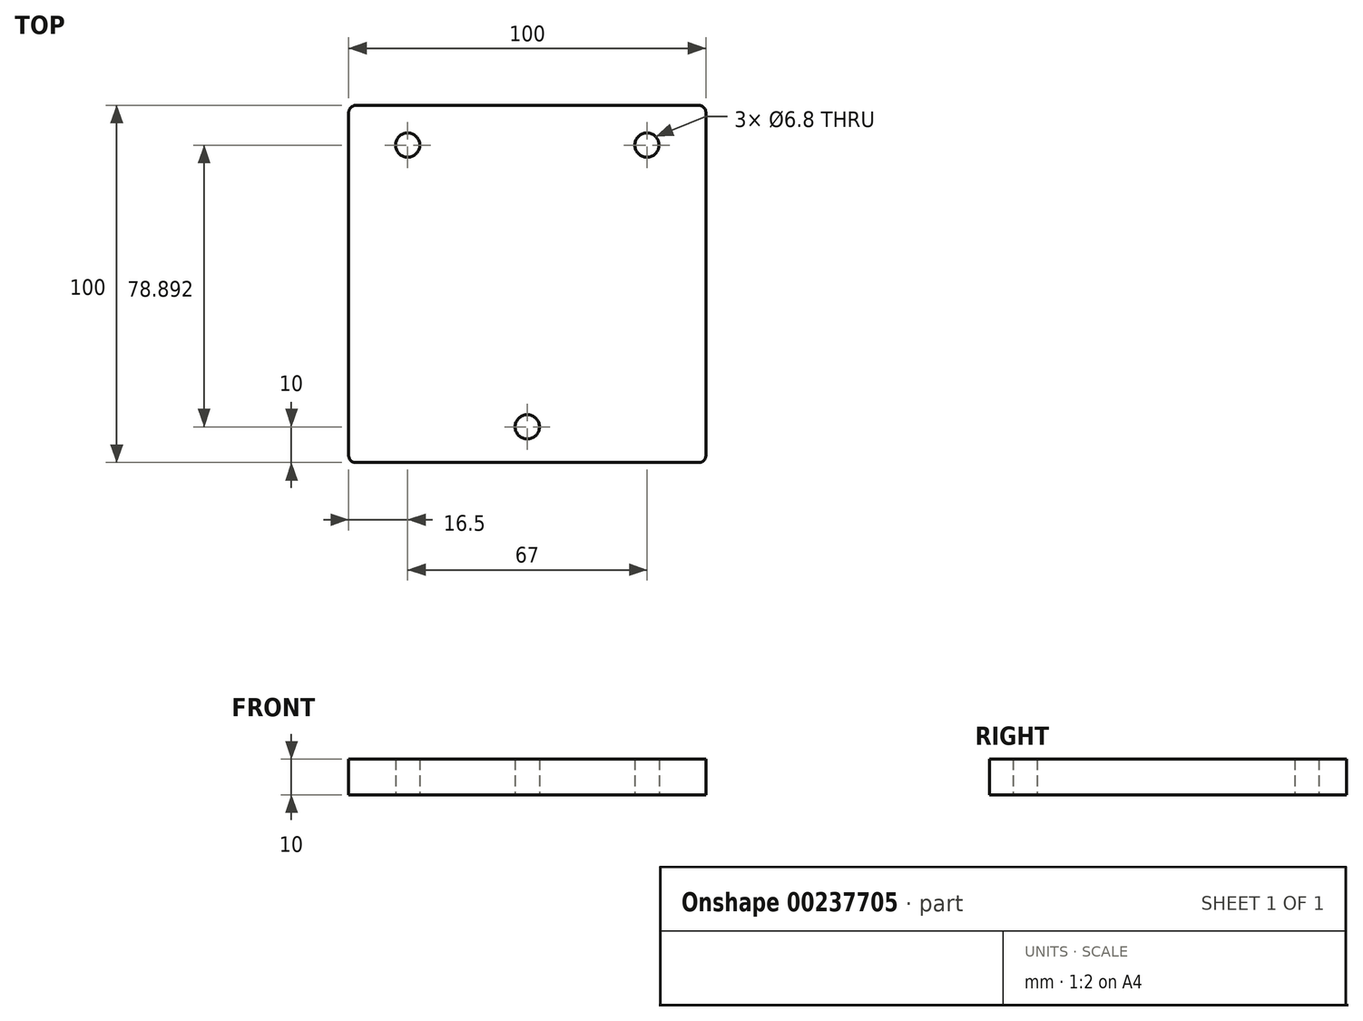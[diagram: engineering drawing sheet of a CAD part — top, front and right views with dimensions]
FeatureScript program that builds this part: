
annotation { "Feature Type Name" : "Feature", "Feature Type Description" : "" }
export const myFeature = defineFeature(function(context is Context, id is Id, definition is map)
    precondition{}
    {
        {
            var Q0;
            Q0=qCreatedBy(makeId("Top.planeOp"),FACE);
            var sketch = newSketch(context, id + "F0", { "sketchPlane" : qUnion([Q0])});
            skLineSegment(sketch, "E0.bottom", {"start": v(48, 50) * mm, "end": v(-48, 50) * mm});
            skLineSegment(sketch, "E0.top", {"start": v(48, -50) * mm, "end": v(-48, -50) * mm});
            skLineSegment(sketch, "E0.left", {"start": v(50, 48) * mm, "end": v(50, -48) * mm});
            skLineSegment(sketch, "E0.right", {"start": v(-50, 48) * mm, "end": v(-50, -48) * mm});
            skPoint(sketch, "E0.middle", {"position": v(0, 0) * mm});
            skPoint(sketch, "E1.visualSharp", {"position": v(-50, 50) * mm});
            skArc(sketch, "E1.filletArc", {"start": v(-48, 50) * mm, "mid": v(-49.41, 49.41) * mm, "end": v(-50, 48) * mm});
            skPoint(sketch, "E2.visualSharp", {"position": v(50, 50) * mm});
            skArc(sketch, "E2.filletArc", {"start": v(50, 48) * mm, "mid": v(49.41, 49.41) * mm, "end": v(48, 50) * mm});
            skPoint(sketch, "E3.visualSharp", {"position": v(50, -50) * mm});
            skArc(sketch, "E3.filletArc", {"start": v(48, -50) * mm, "mid": v(49.41, -49.41) * mm, "end": v(50, -48) * mm});
            skPoint(sketch, "E4.visualSharp", {"position": v(-50, -50) * mm});
            skArc(sketch, "E4.filletArc", {"start": v(-50, -48) * mm, "mid": v(-49.41, -49.41) * mm, "end": v(-48, -50) * mm});
            skCircle(sketch, "E5", {"center": v(-33.5, 38.9) * mm, "radius": 3.4 * mm});
            skCircle(sketch, "E6", {"center": v(33.5, 38.9) * mm, "radius": 3.4 * mm});
            skCircle(sketch, "E7", {"center": v(0, -40) * mm, "radius": 3.4 * mm});
            skSolve(sketch);
        }
        {
            var Q0;
            Q0=makeQuery(id+"F0.imprint","IMPRINT",FACE,{"disambiguationData":[TD([[makeQuery(id+"F0.imprint","IMPRINT",EDGE,{"derivedFrom":sQuery(id+"F0.wireOp",EDGE,"E0.bottom")}),1.0]])]});
            extrude(context, id + "F1", {"entities" : qUnion([Q0]), "depth" : 10 * mm});
        }
    });
